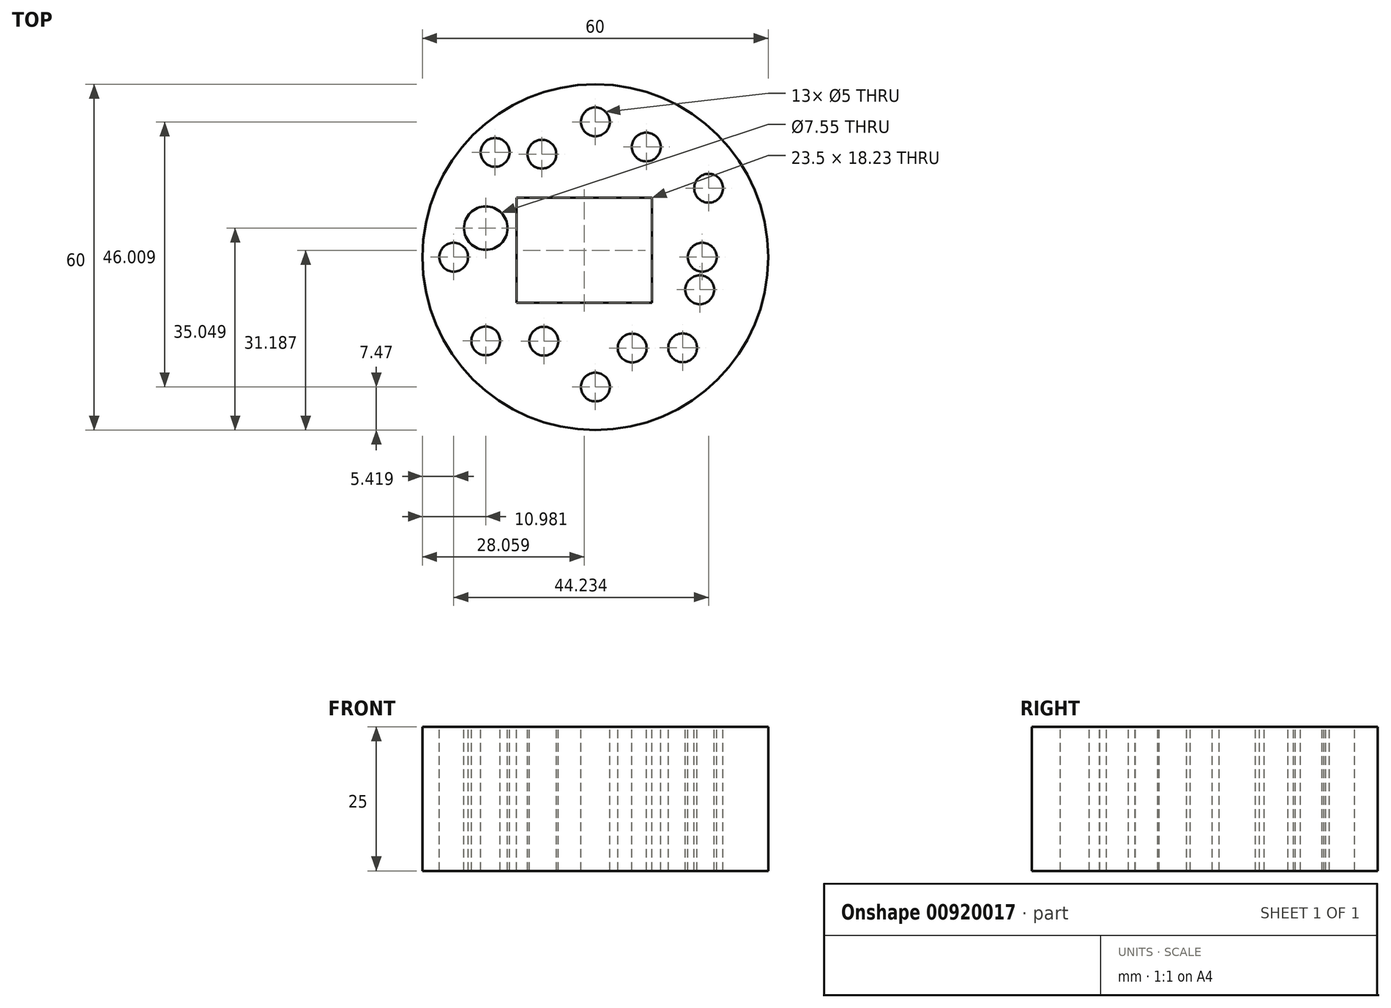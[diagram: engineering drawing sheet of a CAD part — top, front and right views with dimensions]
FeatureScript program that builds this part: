
annotation { "Feature Type Name" : "Feature", "Feature Type Description" : "" }
export const myFeature = defineFeature(function(context is Context, id is Id, definition is map)
    precondition{}
    {
        {
            var Q0;
            Q0=qCreatedBy(makeId("Top.planeOp"),FACE);
            var sketch = newSketch(context, id + "F0", { "sketchPlane" : qUnion([Q0])});
            skCircle(sketch, "E0", {"center": v(0, 0) * mm, "radius": 30 * mm});
            skSolve(sketch);
        }
        {
            var Q0;
            Q0=makeQuery(id+"F0.imprint","IMPRINT",FACE,{"disambiguationData":[TD([[makeQuery(id+"F0.imprint","IMPRINT",EDGE,{"derivedFrom":sQuery(id+"F0.wireOp",EDGE,"E0")}),1.0]])]});
            extrude(context, id + "F1", {"entities" : qUnion([Q0]), "depth" : 25 * mm, "offsetDistance" : 25 * mm});
        }
        {
            var Q0;
            Q0=makeQuery(id+"F1.opExtrude","CAP_FACE",FACE,{"disambiguationData":[OSD([sQuery(id+"F0.wireOp",EDGE,"E0")])],"isStart":false});
            var sketch = newSketch(context, id + "F2", { "sketchPlane" : qUnion([Q0])});
            skLineSegment(sketch, "E1.bottom", {"start": v(-13.7, 10.3) * mm, "end": v(9.8, 10.3) * mm});
            skLineSegment(sketch, "E1.top", {"start": v(-13.7, -7.93) * mm, "end": v(9.8, -7.93) * mm});
            skLineSegment(sketch, "E1.left", {"start": v(-13.7, 10.3) * mm, "end": v(-13.7, -7.93) * mm});
            skLineSegment(sketch, "E1.right", {"start": v(9.8, 10.3) * mm, "end": v(9.8, -7.93) * mm});
            skSolve(sketch);
        }
        {
            var Q0;
            Q0=makeQuery(id+"F2.imprint","IMPRINT",FACE,{"disambiguationData":[TD([[makeQuery(id+"F2.imprint","IMPRINT",EDGE,{"derivedFrom":sQuery(id+"F2.wireOp",EDGE,"E1.bottom")}),-1.0]])]});
            extrude(context, id + "F3", {"entities" : qUnion([Q0]), "operationType" : NewBodyOperationType.ADD, "depth" : -15 * mm, "offsetDistance" : 25 * mm});
        }
        {
            var Q0;
            Q0=makeQuery(id+"F2.imprint","IMPRINT",FACE,{"disambiguationData":[TD([[makeQuery(id+"F2.imprint","IMPRINT",EDGE,{"derivedFrom":sQuery(id+"F2.wireOp",EDGE,"E1.bottom")}),-1.0]])]});
            extrude(context, id + "F4", {"entities" : qUnion([Q0]), "operationType" : NewBodyOperationType.REMOVE, "oppositeDirection" : true, "depth" : 25 * mm, "offsetDistance" : 25 * mm});
        }
        {
            var Q0;
            Q0=makeQuery(id+"F2.imprint","IMPRINT",FACE,{"disambiguationData":[TD([[makeQuery(id+"F2.imprint","IMPRINT",EDGE,{"derivedFrom":sQuery(id+"F2.wireOp",EDGE,"E1.bottom")}),1.0]])]});
            var sketch = newSketch(context, id + "F5", { "sketchPlane" : qUnion([Q0])});
            skCircle(sketch, "E2", {"center": v(0, -22.53) * mm, "radius": 2.5 * mm});
            skCircle(sketch, "E3", {"center": v(18.55, 0) * mm, "radius": 2.5 * mm});
            skCircle(sketch, "E4", {"center": v(8.84, 19.12) * mm, "radius": 2.5 * mm});
            skCircle(sketch, "E5", {"center": v(-19.02, -14.53) * mm, "radius": 2.5 * mm});
            skCircle(sketch, "E6", {"center": v(-19.02, 5.05) * mm, "radius": 3.77 * mm});
            skSolve(sketch);
        }
        {
            var Q0;
            Q0 = qSketchRegion(id + "F5", true);
            extrude(context, id + "F6", {"entities" : qUnion([Q0]), "operationType" : NewBodyOperationType.REMOVE, "oppositeDirection" : true, "depth" : 25 * mm, "offsetDistance" : 25 * mm});
        }
        {
            var Q0;
            Q0=makeQuery(id+"F2.imprint","IMPRINT",FACE,{"disambiguationData":[TD([[makeQuery(id+"F2.imprint","IMPRINT",EDGE,{"derivedFrom":sQuery(id+"F2.wireOp",EDGE,"E1.bottom")}),1.0]])]});
            var sketch = newSketch(context, id + "F7", { "sketchPlane" : qUnion([Q0])});
            skCircle(sketch, "E7", {"center": v(-9.27, 17.88) * mm, "radius": 2.5 * mm});
            skCircle(sketch, "E8", {"center": v(0, 23.48) * mm, "radius": 2.5 * mm});
            skCircle(sketch, "E9", {"center": v(15.15, -15.73) * mm, "radius": 2.5 * mm});
            skSolve(sketch);
        }
        {
            var Q0;
            Q0 = qSketchRegion(id + "F7", true);
            extrude(context, id + "F8", {"entities" : qUnion([Q0]), "operationType" : NewBodyOperationType.REMOVE, "oppositeDirection" : true, "depth" : 25 * mm, "offsetDistance" : 25 * mm});
        }
        {
            var Q0;
            Q0=makeQuery(id+"F2.imprint","IMPRINT",FACE,{"disambiguationData":[TD([[makeQuery(id+"F2.imprint","IMPRINT",EDGE,{"derivedFrom":sQuery(id+"F2.wireOp",EDGE,"E1.bottom")}),1.0]])]});
            var sketch = newSketch(context, id + "F9", { "sketchPlane" : qUnion([Q0])});
            skCircle(sketch, "E10", {"center": v(-8.94, -14.58) * mm, "radius": 2.5 * mm});
            skCircle(sketch, "E11", {"center": v(19.65, 11.97) * mm, "radius": 2.5 * mm});
            skCircle(sketch, "E12", {"center": v(6.39, -15.77) * mm, "radius": 2.5 * mm});
            skCircle(sketch, "E13", {"center": v(-24.58, 0) * mm, "radius": 2.5 * mm});
            skCircle(sketch, "E14", {"center": v(-17.4, 18.18) * mm, "radius": 2.5 * mm});
            skSolve(sketch);
        }
        {
            var Q0;
            Q0 = qSketchRegion(id + "F9", true);
            extrude(context, id + "F10", {"entities" : qUnion([Q0]), "operationType" : NewBodyOperationType.REMOVE, "oppositeDirection" : true, "depth" : 25 * mm, "offsetDistance" : 25 * mm});
        }
        {
            var Q0;
            Q0=makeQuery(id+"F2.imprint","IMPRINT",FACE,{"disambiguationData":[TD([[makeQuery(id+"F2.imprint","IMPRINT",EDGE,{"derivedFrom":sQuery(id+"F2.wireOp",EDGE,"E1.bottom")}),1.0]])]});
            var sketch = newSketch(context, id + "F11", { "sketchPlane" : qUnion([Q0])});
            skCircle(sketch, "E15", {"center": v(18.11, -5.65) * mm, "radius": 2.5 * mm});
            skSolve(sketch);
        }
        {
            var Q0;
            Q0 = qSketchRegion(id + "F11", true);
            extrude(context, id + "F12", {"entities" : qUnion([Q0]), "operationType" : NewBodyOperationType.REMOVE, "oppositeDirection" : true, "depth" : 25 * mm, "offsetDistance" : 25 * mm});
        }
    });
